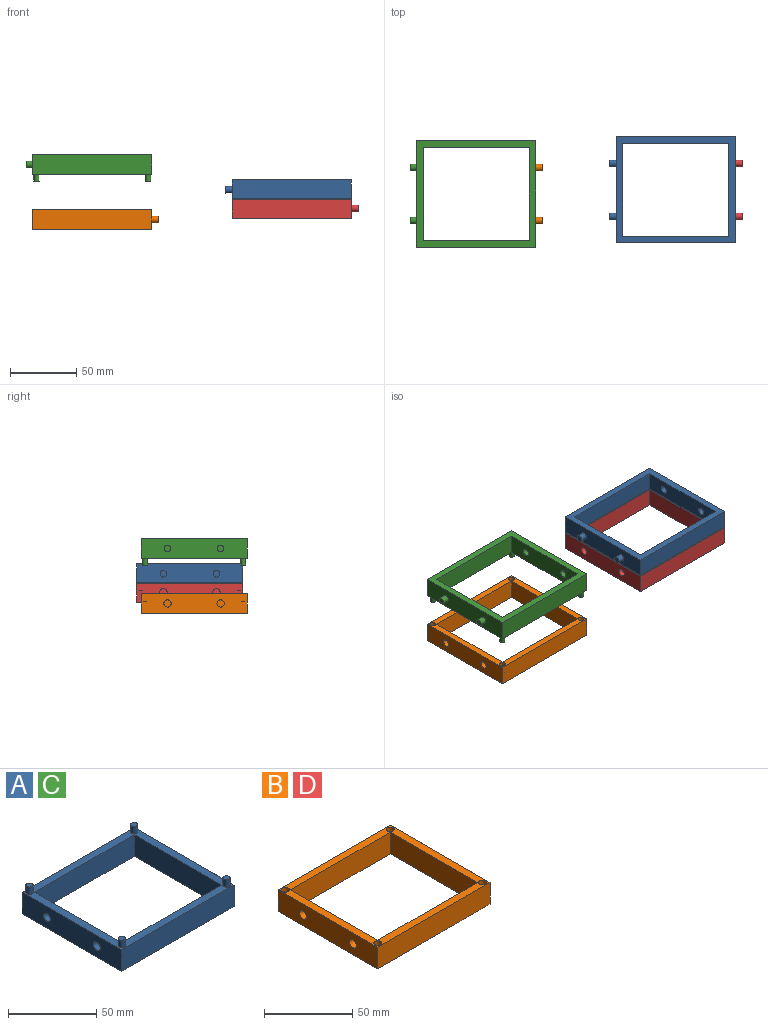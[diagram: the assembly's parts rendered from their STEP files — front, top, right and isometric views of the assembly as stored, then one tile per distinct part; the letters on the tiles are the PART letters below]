
ASSEMBLY  parts=4 mates=2
PART A: 24 faces, bbox 95x80x20 mm
  f0: plane 90x15mm, normal (0,1,0), area 1350mm2, adj f1,f7,f8,f9
  f1: plane 80x15mm, normal (-1,0,0), area 1152.5mm2, adj f0,f2,f8,f9,f18,f19
  f2: plane 90x15mm, normal (0,-1,0), area 1350mm2, adj f1,f7,f8,f9
  f3: plane 70x15mm, normal (1,0,0), area 1002.5mm2, adj f4,f6,f8,f9,f18,f19
  f4: plane 80x15mm, normal (0,-1,0), area 1200mm2, adj f3,f5,f8,f9
  f5: plane 70x15mm, normal (-1,0,0), area 1050mm2, adj f4,f6,f8,f9
  f6: plane 80x15mm, normal (0,1,0), area 1200mm2, adj f3,f5,f8,f9
  f7: plane 80x15mm, normal (1,0,0), area 1160.7mm2, adj f0,f2,f8,f9,f20,f22
  f8: plane 90x80mm, normal (0,0,1), area 1549.7mm2, adj f0,f1,f2,f3,f4,f5,f6,f7
  f9: plane 90x80mm, normal (0,0,-1), area 1600mm2, adj f0,f1,f2,f3,f4,f5,f6,f7
  f10: cylinder r=2mm len=5mm, axis (0,0,-1), area 62.8mm2, adj f8,f11
  f11: plane 4x4mm, normal (0,0,1), area 12.6mm2, adj f10
  f12: cylinder r=2mm len=5mm, axis (0,0,-1), area 62.8mm2, adj f8,f13
  f13: plane 4x4mm, normal (0,0,1), area 12.6mm2, adj f12
  f14: cylinder r=2mm len=5mm, axis (0,0,-1), area 62.8mm2, adj f8,f15
  f15: plane 4x4mm, normal (0,0,1), area 12.6mm2, adj f14
  f16: cylinder r=2mm len=5mm, axis (0,0,-1), area 62.8mm2, adj f8,f17
  f17: plane 4x4mm, normal (0,0,1), area 12.6mm2, adj f16
  f18: cylinder r=2.75mm len=5.5mm, axis (-1,0,0), area 86.4mm2, adj f1,f3
  f19: cylinder r=2.75mm len=5.5mm, axis (-1,0,0), area 86.4mm2, adj f1,f3
  f20: cylinder r=2.5mm len=5mm, axis (-1,0,0), area 78.5mm2, adj f7,f21
  f21: plane 5x5mm, normal (1,0,0), area 19.6mm2, adj f20
  f22: cylinder r=2.5mm len=5mm, axis (-1,0,0), area 78.5mm2, adj f7,f23
  f23: plane 5x5mm, normal (1,0,0), area 19.6mm2, adj f22
PART B: 24 faces, bbox 95x80x15 mm
  f0: plane 90x15mm, normal (0,1,0), area 1350mm2, adj f1,f7,f8,f9
  f1: plane 80x15mm, normal (-1,0,0), area 1152.5mm2, adj f0,f2,f8,f9,f22,f23
  f2: plane 90x15mm, normal (0,-1,0), area 1350mm2, adj f1,f7,f8,f9
  f3: plane 70x15mm, normal (1,0,0), area 1002.5mm2, adj f4,f6,f8,f9,f22,f23
  f4: plane 80x15mm, normal (0,-1,0), area 1200mm2, adj f3,f5,f8,f9
  f5: plane 70x15mm, normal (-1,0,0), area 1050mm2, adj f4,f6,f8,f9
  f6: plane 80x15mm, normal (0,1,0), area 1200mm2, adj f3,f5,f8,f9
  f7: plane 80x15mm, normal (1,0,0), area 1160.7mm2, adj f0,f2,f8,f9,f18,f20
  f8: plane 90x80mm, normal (0,0,1), area 1536.4mm2, adj f0,f1,f2,f3,f4,f5,f6,f7
  f9: plane 90x80mm, normal (0,0,-1), area 1600mm2, adj f0,f1,f2,f3,f4,f5,f6,f7
  f10: cylinder r=2.25mm len=6mm, axis (0,0,1), area 84.8mm2, adj f8,f11
  f11: plane 4.5x4.5mm, normal (0,0,1), area 15.9mm2, adj f10
  f12: cylinder r=2.25mm len=6mm, axis (0,0,1), area 84.8mm2, adj f8,f13
  f13: plane 4.5x4.5mm, normal (0,0,1), area 15.9mm2, adj f12
  f14: cylinder r=2.25mm len=6mm, axis (0,0,1), area 84.8mm2, adj f8,f15
  f15: plane 4.5x4.5mm, normal (0,0,1), area 15.9mm2, adj f14
  f16: cylinder r=2.25mm len=6mm, axis (0,0,1), area 84.8mm2, adj f8,f17
  f17: plane 4.5x4.5mm, normal (0,0,1), area 15.9mm2, adj f16
  f18: cylinder r=2.5mm len=5mm, axis (-1,0,0), area 78.5mm2, adj f7,f19
  f19: plane 5x5mm, normal (1,0,0), area 19.6mm2, adj f18
  f20: cylinder r=2.5mm len=5mm, axis (-1,0,0), area 78.5mm2, adj f7,f21
  f21: plane 5x5mm, normal (1,0,0), area 19.6mm2, adj f20
  f22: cylinder r=2.75mm len=5.5mm, axis (-1,0,0), area 86.4mm2, adj f1,f3
  f23: cylinder r=2.75mm len=5.5mm, axis (-1,0,0), area 86.4mm2, adj f1,f3
PART C: same geometry as A
PART D: same geometry as B
PLACE A rot(axis=(0,1,0),180deg) t=(157.81,-70.6,147.08)mm
PLACE B t=(-82.54,-73.75,109.68)mm fixed
PLACE C rot(axis=(0,1,0),180deg) t=(7.46,-73.75,166.12)mm
PLACE D rot(axis=(0,-1,0),0deg) t=(67.81,-70.6,118.08)mm fixed
MATE slider C.f10 <-> B.f12  axis (0,0,-1) through (4.46,3.25,146.12)mm
MATE fastened D.f12 <-> A.f10  axis (0,0,1) through (154.81,6.4,127.08)mm
